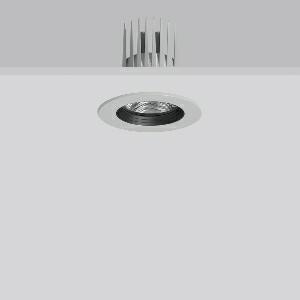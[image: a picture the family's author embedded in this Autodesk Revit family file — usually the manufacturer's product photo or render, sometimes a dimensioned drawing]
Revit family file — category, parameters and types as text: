
# Revit family: heledon_mini_e_901742_004_1_45d1
name_source: partatom
category: Lighting Fixtures
units: mm (PartAtom-declared; Revit-internal decimal feet)

## family parameters
Cut with Voids When Loaded = No
Host = Face
Light Source = No
Part Type = Normal
Room Calculation Point = No
Round Connector Dimension = Use Diameter
Shared = No

## types (1)
- HELEDON mini E (1 x LED Modul 940, 2750 lm, 4000)
    Apparent Load = 20 VA
    Approval mark = CE
    CIE Flux Codes = 95 99 100 100 100
    Color Rendering = 92
    Color Temperature = 4000
    Default Elevation = 1800 mm
    Description = Series: HELEDON mini
Round recessed downlight. Housing: die-cast aluminium, powder-coated. Black plastic ring and recessed LED to prevent glare from the side. Optical assembly with reflector made of MIRO-Silver with 98% total light reflection for outstanding efficiency - can be changed without tools. Best colour rendering index Ra>90. Suitable for Recessed ceiling mounting. Installation without tools thanks to spring fastening system. Including separate LED converter with connecting cable 600 mm.High quality converter without flickering and stroboscopic effect. Through-wiring box (5 pole) available as accessory. The following accessories can be mounted without use of tools: interchangeable lenses, decorative glasses, honeycomb louvre, clear and frosted diffusers, white interchangeable plastic ring. 
Colour: silver
Diameter: 124 mm
Height: 3 mm
Cut-out diameter: 114 mm
Recess height: 170 mm
Luminaire: recess height: 120 mm
Lamp: LED
Socket: without socket
Colour temperature: 4000K
Colour rendering index (CRI): 92
System power: 20 W
Rated luminous flux: 2750 lm
Luminous efficiency: 138 lm/W
Control gear: Regulated power supply
Protection class: II
Type of protection: IP 20
    Height = 0 mm  [stored 0 ft]
    Lamp = 1 x LED Modul 940
    Lamp Light Flux = 2750 lm
    Lamp count = 1
    Length = 124 mm  [stored 0.406824 ft]
    Lifetime = 50000 h
    Luminous efficacy = 138 lm/W
    Manufacturer = RZB
    ModVariant = No
    Model = 901742.004.1
    Mounting Place = Ceiling
    Mounting Type = Recessed
    Number of Poles = 1
    OnlyDefault = Yes
    Power Factor = 1
    Product Name = HELEDON mini E
    Product group = Recessed downlights
    ProductGroupID = 402
    Protection Class = Protection class II
    Protection Degree = IP 20
    RLX_Detail_Level = 1
    RLX_Emergency_Light_Flux = 0 lm
    RLX_Emergency_Type = 0
    RLX_Emergency_Type_DB = No
    RlxData = <blob elided: 126553 chars, md5=38403419>
    Socket = socket
    Standby Power = 0 W
    System Light Flux = 2750 lm
    System Power = 20 W
    Type Comments = Product without accessories
    Type Image = 901657.004.jpg
    URL = http://relux.com
    VarID = ---
    Voltage = 230 V
    Voltage Range = 220-240 V
    Weight = 0.00 kg
    Width = 0 mm  [stored 0 ft]

note: [stored X ft] marks values corroborated as IEEE doubles in the binary element streams (Revit-internal decimal feet)

## geometry (parser evidence)
native form markers: Blend x4, Sweep x10
no freeform markers — native parametric forms only
